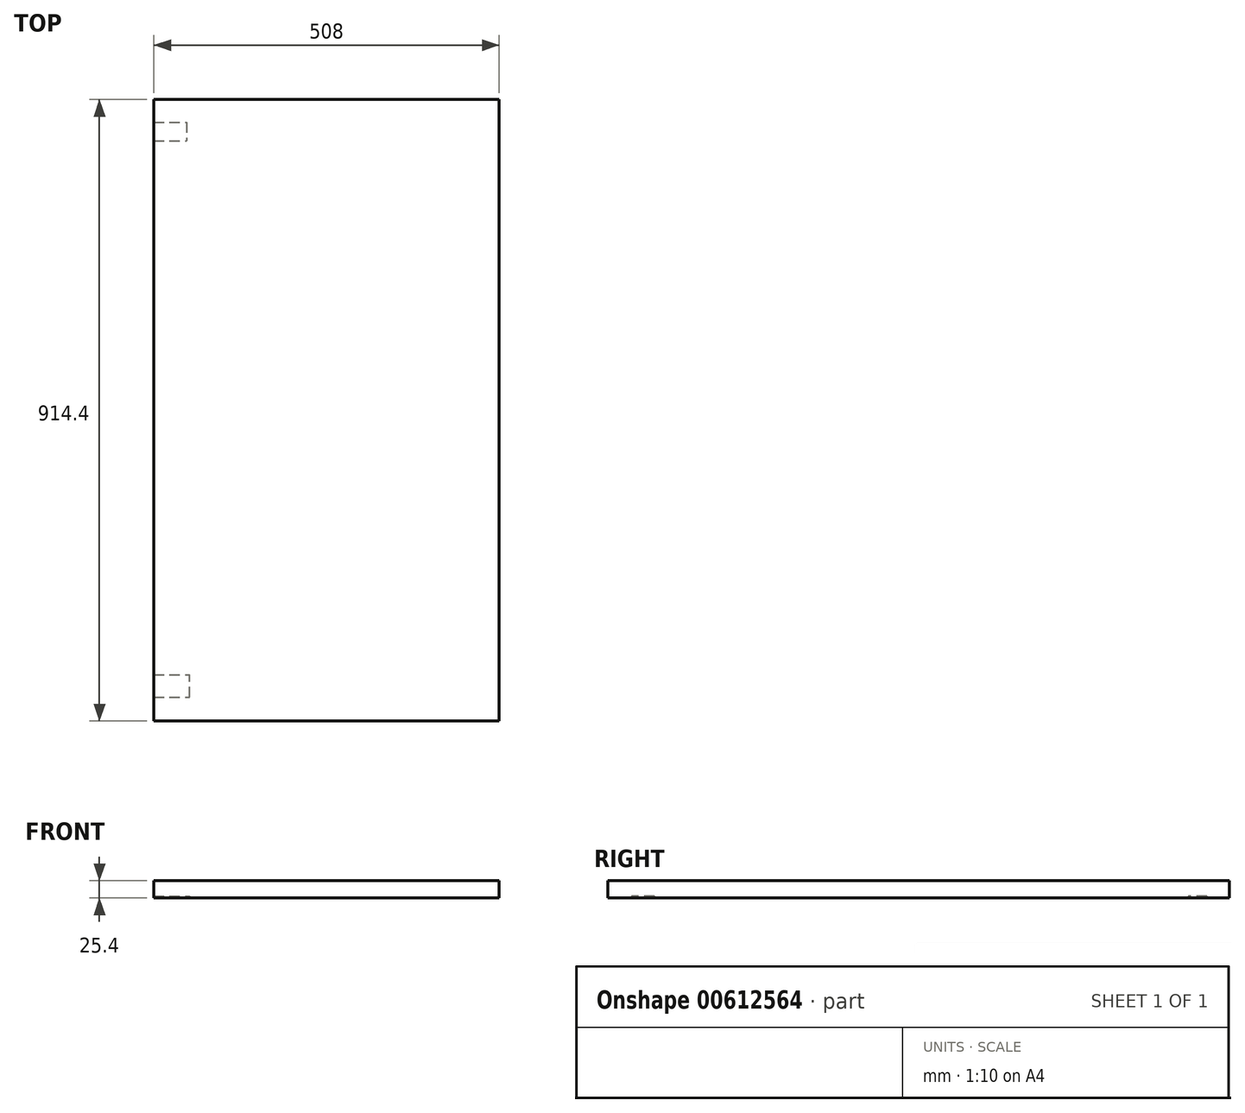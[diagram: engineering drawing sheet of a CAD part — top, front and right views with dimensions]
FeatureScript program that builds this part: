
annotation { "Feature Type Name" : "Feature", "Feature Type Description" : "" }
export const myFeature = defineFeature(function(context is Context, id is Id, definition is map)
    precondition{}
    {
        {
            var Q0;
            Q0=qCreatedBy(makeId("Top.planeOp"),FACE);
            var sketch = newSketch(context, id + "F0", { "sketchPlane" : qUnion([Q0])});
            skLineSegment(sketch, "E0.bottom", {"start": v(-160.77, 498.73) * mm, "end": v(347.23, 498.73) * mm});
            skLineSegment(sketch, "E0.top", {"start": v(-160.77, -415.67) * mm, "end": v(347.23, -415.67) * mm});
            skLineSegment(sketch, "E0.left", {"start": v(-160.77, 498.73) * mm, "end": v(-160.77, -415.67) * mm});
            skLineSegment(sketch, "E0.right", {"start": v(347.23, 498.73) * mm, "end": v(347.23, -415.67) * mm});
            skSolve(sketch);
        }
        {
            var Q0;
            Q0=makeQuery(id+"F0.imprint","IMPRINT",FACE,{"disambiguationData":[TD([[makeQuery(id+"F0.imprint","IMPRINT",EDGE,{"derivedFrom":sQuery(id+"F0.wireOp",EDGE,"E0.bottom")}),-1.0]])]});
            extrude(context, id + "F1", {"entities" : qUnion([Q0]), "depth" : 25.4 * mm, "offsetDistance" : 25.4 * mm});
        }
        {
            var Q0;
            Q0=makeQuery(id+"F1.opExtrude","CAP_FACE",FACE,{"disambiguationData":[OSD([sQuery(id+"F0.wireOp",EDGE,"E0.bottom"),sQuery(id+"F0.wireOp",EDGE,"E0.top"),sQuery(id+"F0.wireOp",EDGE,"E0.left"),sQuery(id+"F0.wireOp",EDGE,"E0.right")])],"isStart":true});
            var sketch = newSketch(context, id + "F2", { "sketchPlane" : qUnion([Q0])});
            skLineSegment(sketch, "E1.bottom", {"start": v(-160.77, 380.62) * mm, "end": v(-108.41, 380.62) * mm});
            skLineSegment(sketch, "E1.top", {"start": v(-160.77, 347.52) * mm, "end": v(-108.41, 347.52) * mm});
            skLineSegment(sketch, "E1.left", {"start": v(-160.77, 380.62) * mm, "end": v(-160.77, 347.52) * mm});
            skLineSegment(sketch, "E1.right", {"start": v(-108.41, 380.62) * mm, "end": v(-108.41, 347.52) * mm});
            skSolve(sketch);
        }
        {
            var Q0;
            Q0=makeQuery(id+"F2.imprint","IMPRINT",FACE,{"disambiguationData":[TD([[makeQuery(id+"F2.imprint","IMPRINT",EDGE,{"derivedFrom":sQuery(id+"F2.wireOp",EDGE,"E1.bottom")}),-1.0]])]});
            extrude(context, id + "F3", {"entities" : qUnion([Q0]), "operationType" : NewBodyOperationType.REMOVE, "oppositeDirection" : true, "depth" : 2.54 * mm, "offsetDistance" : 25.4 * mm});
        }
        {
            var Q0;
            Q0=makeQuery(id+"F1.opExtrude","CAP_FACE",FACE,{"disambiguationData":[OSD([sQuery(id+"F0.wireOp",EDGE,"E0.bottom"),sQuery(id+"F0.wireOp",EDGE,"E0.top"),sQuery(id+"F0.wireOp",EDGE,"E0.left"),sQuery(id+"F0.wireOp",EDGE,"E0.right")])],"isStart":true});
            var sketch = newSketch(context, id + "F4", { "sketchPlane" : qUnion([Q0])});
            skLineSegment(sketch, "E2.bottom", {"start": v(-160.77, -465.29) * mm, "end": v(-112.43, -465.29) * mm});
            skLineSegment(sketch, "E2.top", {"start": v(-160.77, -438.02) * mm, "end": v(-112.43, -438.02) * mm});
            skLineSegment(sketch, "E2.left", {"start": v(-160.77, -465.29) * mm, "end": v(-160.77, -438.02) * mm});
            skLineSegment(sketch, "E2.right", {"start": v(-112.43, -465.29) * mm, "end": v(-112.43, -438.02) * mm});
            skSolve(sketch);
        }
        {
            var Q0;
            Q0=makeQuery(id+"F4.imprint","IMPRINT",FACE,{"disambiguationData":[TD([[makeQuery(id+"F4.imprint","IMPRINT",EDGE,{"derivedFrom":sQuery(id+"F4.wireOp",EDGE,"E2.bottom")}),1.0]])]});
            extrude(context, id + "F5", {"entities" : qUnion([Q0]), "operationType" : NewBodyOperationType.REMOVE, "oppositeDirection" : true, "depth" : 2.54 * mm, "offsetDistance" : 25.4 * mm});
        }
    });
